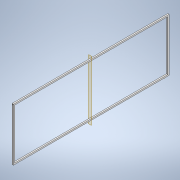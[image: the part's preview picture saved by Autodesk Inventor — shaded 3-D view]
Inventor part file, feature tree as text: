
AUTODESK INVENTOR PART (.ipt)
format: ipt  version: 2022 (Build 260153000, 153)  size: 184,832 bytes
history: native  units: mm
features: extrude x7, sketch x7, projected_geometry x3, plane x2, mirror x2, fillet x1
ambient origin geometry x8: Origin, YZ Plane, XZ Plane, XY Plane, X Axis, Y Axis, Z Axis, Center Point
bodies: Solid1 (feature_tree)
feature tree (22):
  extrude  "Extrusion1"  Depth=1138.0mm
  extrude  "Extrusion2"  Depth=10.0mm TaperAngle=0.0deg
  plane  "Work Plane1"
  mirror  "Mirror1"
  fillet  "Fillet1"  Radius=4.5mm
  plane  "Work Plane2"
  extrude  "Extrusion3"  Depth=1.0mm
  extrude  "Extrusion4"  Depth=10.0mm
  extrude  "Extrusion5"  [1 undecoded]
  extrude  "Extrusion6"  Depth=10.0mm TaperAngle=0.0deg
  extrude  "Extrusion7"  Depth=5.0mm
  mirror  "Mirror2"
  sketch  "Sketch1"  dims[d0=383.0mm d1=1138.0mm]
  sketch  "Sketch2"  dims[d2=10.0mm d3=10.0mm d4=0.0mm d5=4.5mm]
  projected_geometry  "Projected Loop1"
  sketch  "Sketch3"  dims[d6=135.0deg d7=1.0mm]
  sketch  "Sketch4"  dims[d8=35.0mm d9=0.0mm d10=10.0mm]
  sketch  "Sketch5"  dims[d11=2.0mm d12=-10.0mm]
  sketch  "Sketch6"  dims[d13=15.0mm d14=0.0mm d15=10.0mm d16=0.0mm]
  projected_geometry  "Projected Loop2"
  sketch  "Sketch7"  dims[d17=10.0mm d18=0.0mm d19=5.0mm d20=3.0mm d21=0.0mm d22=15.0mm d23=5.0mm d24=0.0mm d25=26.0mm d26=26.0mm]
  projected_geometry  "Projected Loop3"
note: 1 required parameter value undecoded (feature->parameter linkage not recoverable at this tier; creation-order binding heuristic only, values carry confidence <= 0.55)
